# Revit family: Borgo Trimless 200 2700K
name_source: partatom
category: Lighting Fixtures
revit_build: Autodesk Revit 2018 (Build: 20170223_1515(x64)
units: mm (PartAtom-declared; Revit-internal decimal feet)

## family parameters
Always vertical = Yes
Cut with Voids When Loaded = Yes
Host = Wall
Light Source = Yes
OmniClass Number = 23.80.70.00
OmniClass Title = Lighting
Part Type = Normal
Room Calculation Point = No
Round Connector Dimension = Use Diameter
Shared = No

## types (2) — shared parameters
Color Filter = 16777215
Dimming Lamp Color Temperature Shift = <None>
Main Material = Metal - Steel
Manufacturer = Astro Lighting Ltd
URL = www.astrolighting.com

## per-type parameters (varying)
| type | ADA compliant | Driver Required | Electrical Class | Location rating | Photometric Web File | Product Code | Product Location | Product SKU | Tilt Angle | aperture height |
| CE |  | Yes | 3 |  | GNC-19573  7626 - Borgo Trimless 200 2700K ies.ies | 7626 |  | 1212040 | 0.00° | 201 mm  [stored 0.659449 ft] |
| ETL | NO | No | 0 | DAMP | generic | 1234 | Bathroom | 1234001 | 60.00° | 67 mm |

note: [stored X ft] marks values corroborated as IEEE doubles in the binary element streams (Revit-internal decimal feet)

## geometry (parser evidence)
native form markers: Sweep x2
no freeform markers — native parametric forms only
